# Revit family: 205_SIBL-_-1200
name_source: partatom
category: Duct Accessories
units: mm (PartAtom-declared; Revit-internal decimal feet)

## family parameters
Always vertical = Yes
Cut with Voids When Loaded = No
Part Type = Breaks Into
Round Connector Dimension = Use Diameter
Shared = No
Work Plane-Based = No

## types (5) — shared parameters
Description = CIRCULAR SILENCER WITH CORE
L1 = 7 mm  [stored 0.0229659 ft]
L2 = 1186 mm  [stored 3.89108 ft]
L2D = 1200 mm
LL = 600 mm  [stored 1.9685 ft]
Manufacturer = Alnor
QmdConnectorList = 201;D;202;D
URL = http://www.ventilation-alnor.co.uk
magiPartTypeId = 205
magiProductFamilyId = SIBL-*-1200

## per-type parameters (varying)
| type | CD1 | CD2 | D | H2D | R | W2D |
| SIBL-315-1200 | 250 mm  [stored 0.82021 ft] | 251 mm  [stored 0.823491 ft] | 315 mm | 515 mm | 158 mm | 515 mm |
| SIBL-800-1200 | 500 mm  [stored 1.64042 ft] | 501 mm | 800 mm | 1000 mm  [stored 3.28084 ft] | 400 mm | 1000 mm  [stored 3.28084 ft] |
| SIBL-630-1200 | 400 mm | 401 mm | 630 mm | 830 mm | 315 mm  [stored 1.03346 ft] | 830 mm |
| SIBL-500-1200 | 355 mm | 356 mm | 500 mm | 700 mm | 250 mm  [stored 0.82021 ft] | 700 mm |
| SIBL-400-1200 | 300 mm  [stored 0.984252 ft] | 301 mm | 400 mm | 600 mm  [stored 1.9685 ft] | 200 mm | 600 mm  [stored 1.9685 ft] |

note: column(s) folded — value = type name in every type: MC Product Code, magiProductId

note: [stored X ft] marks values corroborated as IEEE doubles in the binary element streams (Revit-internal decimal feet)

## geometry (parser evidence)
native form markers: Blend x4, Sweep x1
no freeform markers — native parametric forms only
